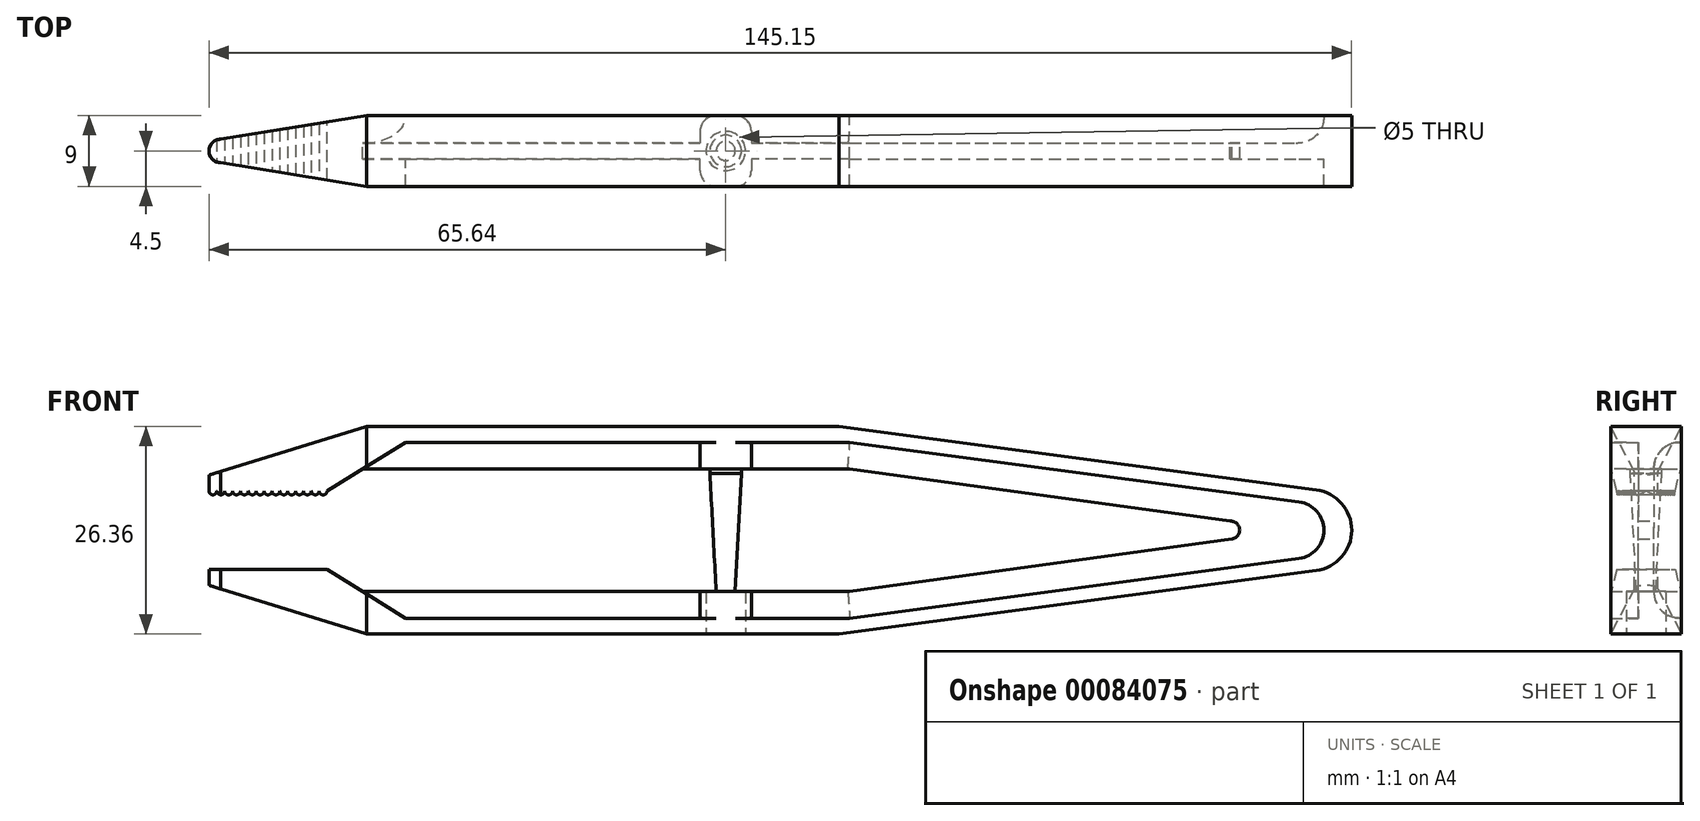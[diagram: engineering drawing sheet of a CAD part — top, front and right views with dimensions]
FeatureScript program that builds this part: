
annotation { "Feature Type Name" : "Feature", "Feature Type Description" : "" }
export const myFeature = defineFeature(function(context is Context, id is Id, definition is map)
    precondition{}
    {
        {
            var Q0;
            Q0=qCreatedBy(makeId("Front.planeOp"),FACE);
            var sketch = newSketch(context, id + "F0", { "sketchPlane" : qUnion([Q0])});
            skLineSegment(sketch, "E0", {"start": v(-60.1, 0) * mm, "end": v(64.63, 0) * mm});
            skLineSegment(sketch, "E1", {"start": v(-65.64, 7) * mm, "end": v(-45.64, 13.18) * mm});
            skLineSegment(sketch, "E2", {"start": v(-45.64, 13.18) * mm, "end": v(14.36, 13.18) * mm});
            skLineSegment(sketch, "E3", {"start": v(14.36, 13.18) * mm, "end": v(75.04, 5.1) * mm});
            skLineSegment(sketch, "E4", {"start": v(-65.64, 7) * mm, "end": v(-65.64, 5) * mm});
            skLineSegment(sketch, "E5", {"start": v(-65.64, 5) * mm, "end": v(-50.64, 5) * mm});
            skLineSegment(sketch, "E6", {"start": v(-50.64, 5) * mm, "end": v(-40.69, 11.18) * mm});
            skLineSegment(sketch, "E7", {"start": v(-40.69, 11.18) * mm, "end": v(15.75, 11.18) * mm});
            skLineSegment(sketch, "E8", {"start": v(15.75, 11.18) * mm, "end": v(72.84, 3.59) * mm});
            skLineSegment(sketch, "E9.MirrorCS", {"start": v(-65.64, -7) * mm, "end": v(-65.64, -5) * mm});
            skLineSegment(sketch, "E10.MirrorCS", {"start": v(-65.64, -5) * mm, "end": v(-50.64, -5) * mm});
            skLineSegment(sketch, "E11.MirrorCS", {"start": v(-45.64, -13.18) * mm, "end": v(14.36, -13.18) * mm});
            skLineSegment(sketch, "E12.MirrorCS", {"start": v(-40.69, -11.18) * mm, "end": v(15.75, -11.18) * mm});
            skLineSegment(sketch, "E13.MirrorCS", {"start": v(14.36, -13.18) * mm, "end": v(75.04, -5.1) * mm});
            skLineSegment(sketch, "E14.MirrorCS", {"start": v(-50.64, -5) * mm, "end": v(-40.69, -11.18) * mm});
            skLineSegment(sketch, "E15.MirrorCS", {"start": v(-65.64, -7) * mm, "end": v(-45.64, -13.18) * mm});
            skLineSegment(sketch, "E16.MirrorCS", {"start": v(15.75, -11.18) * mm, "end": v(72.84, -3.59) * mm});
            skArc(sketch, "E17", {"start": v(75.04, -5.1) * mm, "mid": v(79.51, 0) * mm, "end": v(75.04, 5.1) * mm});
            skArc(sketch, "E18", {"start": v(72.84, -3.59) * mm, "mid": v(75.98, 0) * mm, "end": v(72.84, 3.59) * mm});
            skLineSegment(sketch, "E19", {"start": v(15.75, 7.8) * mm, "end": v(-46.13, 7.8) * mm});
            skLineSegment(sketch, "E20", {"start": v(15.75, 7.8) * mm, "end": v(72.36, 0) * mm});
            skLineSegment(sketch, "E21.MirrorCS", {"start": v(15.75, -7.8) * mm, "end": v(-46.13, -7.8) * mm});
            skLineSegment(sketch, "E22.MirrorCS", {"start": v(15.75, -7.8) * mm, "end": v(72.36, 0) * mm});
            skArc(sketch, "E23", {"start": v(64.28, -1.11) * mm, "mid": v(65.28, 0.14) * mm, "end": v(64.03, 1.15) * mm});
            skSolve(sketch);
        }
        {
            var Q0;
            Q0=makeQuery(id+"F0.imprint","IMPRINT",FACE,{"disambiguationData":[TD([[makeQuery(id+"F0.imprint","IMPRINT",EDGE,{"derivedFrom":sQuery(id+"F0.wireOp",EDGE,"E1")}),-1.0]])]});
            extrude(context, id + "F1", {"entities" : qUnion([Q0]), "endBound" : BoundingType.SYMMETRIC, "depth" : 9 * mm});
        }
        {
            var Q0;
            {var subQ10=sQuery(id+"F0.wireOp",EDGE,"E7");Q0=makeQuery(id+"F0.imprint","IMPRINT",FACE,{"disambiguationData":[TD([[makeQuery(id+"F0.imprint","IMPRINT",EDGE,{"derivedFrom":subQ10}),-1.0]])]});}
            var Q1;
            {var subQ0=sQuery(id+"F0.wireOp",EDGE,"E22.MirrorCS");var subQ1=sQuery(id+"F0.wireOp",EDGE,"E20");var subQ2=makeQuery(id+"F0.imprint","INTERSECT",VERTEX,{"derivedFrom":[subQ1,subQ0]});Q1=makeQuery(id+"F0.imprint","IMPRINT",FACE,{"disambiguationData":[TD([[makeQuery(id+"F0.imprint","IMPRINT",EDGE,{"disambiguationData":[TD([[subQ2,1.0]])],"derivedFrom":subQ1}),-1.0]])]});}
            extrude(context, id + "F2", {"entities" : qUnion([Q0, Q1]), "operationType" : NewBodyOperationType.ADD, "endBound" : BoundingType.SYMMETRIC, "depth" : 2 * mm});
        }
        {
            var Q0;
            Q0=makeQuery(id+"F1.opExtrude","CAP_FACE",FACE,{"disambiguationData":[OSD([sQuery(id+"F0.wireOp",EDGE,"E1"),sQuery(id+"F0.wireOp",EDGE,"E2"),sQuery(id+"F0.wireOp",EDGE,"E3"),sQuery(id+"F0.wireOp",EDGE,"E4"),sQuery(id+"F0.wireOp",EDGE,"E5"),sQuery(id+"F0.wireOp",EDGE,"E6"),sQuery(id+"F0.wireOp",EDGE,"E7"),sQuery(id+"F0.wireOp",EDGE,"E8"),sQuery(id+"F0.wireOp",EDGE,"E9.MirrorCS"),sQuery(id+"F0.wireOp",EDGE,"E10.MirrorCS"),sQuery(id+"F0.wireOp",EDGE,"E11.MirrorCS"),sQuery(id+"F0.wireOp",EDGE,"E12.MirrorCS"),sQuery(id+"F0.wireOp",EDGE,"E13.MirrorCS"),sQuery(id+"F0.wireOp",EDGE,"E14.MirrorCS"),sQuery(id+"F0.wireOp",EDGE,"E15.MirrorCS"),sQuery(id+"F0.wireOp",EDGE,"E16.MirrorCS"),sQuery(id+"F0.wireOp",EDGE,"E17"),sQuery(id+"F0.wireOp",EDGE,"E18")])],"isStart":false});
            var sketch = newSketch(context, id + "F3", { "sketchPlane" : qUnion([Q0])});
            skLineSegment(sketch, "E24", {"start": v(-29.66, 0) * mm, "end": v(-67.82, 0) * mm});
            skArc(sketch, "E25", {"start": v(-65.64, 5) * mm, "mid": v(-65.14, 4.5) * mm, "end": v(-64.64, 5) * mm});
            skArc(sketch, "E26.1.0.0", {"start": v(-64.64, 5) * mm, "mid": v(-64.14, 4.5) * mm, "end": v(-63.64, 5) * mm});
            skArc(sketch, "E26.2.0.0", {"start": v(-63.64, 5) * mm, "mid": v(-63.14, 4.5) * mm, "end": v(-62.64, 5) * mm});
            skArc(sketch, "E26.3.0.0", {"start": v(-62.64, 5) * mm, "mid": v(-62.14, 4.5) * mm, "end": v(-61.64, 5) * mm});
            skArc(sketch, "E26.4.0.0", {"start": v(-61.64, 5) * mm, "mid": v(-61.14, 4.5) * mm, "end": v(-60.64, 5) * mm});
            skArc(sketch, "E26.5.0.0", {"start": v(-60.64, 5) * mm, "mid": v(-60.14, 4.5) * mm, "end": v(-59.64, 5) * mm});
            skArc(sketch, "E26.6.0.0", {"start": v(-59.64, 5) * mm, "mid": v(-59.14, 4.5) * mm, "end": v(-58.64, 5) * mm});
            skArc(sketch, "E26.7.0.0", {"start": v(-58.64, 5) * mm, "mid": v(-58.14, 4.5) * mm, "end": v(-57.64, 5) * mm});
            skArc(sketch, "E26.8.0.0", {"start": v(-57.64, 5) * mm, "mid": v(-57.14, 4.5) * mm, "end": v(-56.64, 5) * mm});
            skArc(sketch, "E26.9.0.0", {"start": v(-56.64, 5) * mm, "mid": v(-56.14, 4.5) * mm, "end": v(-55.64, 5) * mm});
            skArc(sketch, "E26.10.0.0", {"start": v(-55.64, 5) * mm, "mid": v(-55.14, 4.5) * mm, "end": v(-54.64, 5) * mm});
            skArc(sketch, "E26.11.0.0", {"start": v(-54.64, 5) * mm, "mid": v(-54.14, 4.5) * mm, "end": v(-53.64, 5) * mm});
            skArc(sketch, "E26.12.0.0", {"start": v(-53.64, 5) * mm, "mid": v(-53.14, 4.5) * mm, "end": v(-52.64, 5) * mm});
            skArc(sketch, "E26.13.0.0", {"start": v(-52.64, 5) * mm, "mid": v(-52.14, 4.5) * mm, "end": v(-51.64, 5) * mm});
            skArc(sketch, "E26.14.0.0", {"start": v(-51.64, 5) * mm, "mid": v(-51.14, 4.5) * mm, "end": v(-50.64, 5) * mm});
            skLineSegment(sketch, "E26.direction1", {"start": v(-65.64, 5) * mm, "end": v(-64.64, 5) * mm, "construction": true});
            skLineSegment(sketch, "E27.MirrorCS", {"start": v(-65.64, -5) * mm, "end": v(-64.64, -5) * mm, "construction": true});
            skArc(sketch, "E28.MirrorCS", {"start": v(-53.64, -5) * mm, "mid": v(-53.14, -4.5) * mm, "end": v(-52.64, -5) * mm});
            skArc(sketch, "E29.MirrorCS", {"start": v(-52.64, -5) * mm, "mid": v(-52.14, -4.5) * mm, "end": v(-51.64, -5) * mm});
            skArc(sketch, "E30.MirrorCS", {"start": v(-51.64, -5) * mm, "mid": v(-51.14, -4.5) * mm, "end": v(-50.64, -5) * mm});
            skArc(sketch, "E31.MirrorCS", {"start": v(-65.64, -5) * mm, "mid": v(-65.14, -4.5) * mm, "end": v(-64.64, -5) * mm});
            skArc(sketch, "E32.MirrorCS", {"start": v(-64.64, -5) * mm, "mid": v(-64.14, -4.5) * mm, "end": v(-63.64, -5) * mm});
            skArc(sketch, "E33.MirrorCS", {"start": v(-63.64, -5) * mm, "mid": v(-63.14, -4.5) * mm, "end": v(-62.64, -5) * mm});
            skArc(sketch, "E34.MirrorCS", {"start": v(-62.64, -5) * mm, "mid": v(-62.14, -4.5) * mm, "end": v(-61.64, -5) * mm});
            skArc(sketch, "E35.MirrorCS", {"start": v(-61.64, -5) * mm, "mid": v(-61.14, -4.5) * mm, "end": v(-60.64, -5) * mm});
            skArc(sketch, "E36.MirrorCS", {"start": v(-60.64, -5) * mm, "mid": v(-60.14, -4.5) * mm, "end": v(-59.64, -5) * mm});
            skArc(sketch, "E37.MirrorCS", {"start": v(-59.64, -5) * mm, "mid": v(-59.14, -4.5) * mm, "end": v(-58.64, -5) * mm});
            skArc(sketch, "E38.MirrorCS", {"start": v(-58.64, -5) * mm, "mid": v(-58.14, -4.5) * mm, "end": v(-57.64, -5) * mm});
            skArc(sketch, "E39.MirrorCS", {"start": v(-57.64, -5) * mm, "mid": v(-57.14, -4.5) * mm, "end": v(-56.64, -5) * mm});
            skArc(sketch, "E40.MirrorCS", {"start": v(-56.64, -5) * mm, "mid": v(-56.14, -4.5) * mm, "end": v(-55.64, -5) * mm});
            skArc(sketch, "E41.MirrorCS", {"start": v(-55.64, -5) * mm, "mid": v(-55.14, -4.5) * mm, "end": v(-54.64, -5) * mm});
            skArc(sketch, "E42.MirrorCS", {"start": v(-54.64, -5) * mm, "mid": v(-54.14, -4.5) * mm, "end": v(-53.64, -5) * mm});
            skSolve(sketch);
        }
        {
            var Q0;
            {var subQ0=sQuery(id+"F3.wireOp",EDGE,"E25");Q0=makeQuery(id+"F3.imprint","IMPRINT",FACE,{"disambiguationData":[TD([[makeQuery(id+"F3.imprint","IMPRINT",EDGE,{"derivedFrom":subQ0}),1.0]])]});}
            var Q1;
            {var subQ0=sQuery(id+"F3.wireOp",EDGE,"E26.1.0.0");Q1=makeQuery(id+"F3.imprint","IMPRINT",FACE,{"disambiguationData":[TD([[makeQuery(id+"F3.imprint","IMPRINT",EDGE,{"derivedFrom":subQ0}),1.0]])]});}
            var Q2;
            {var subQ0=sQuery(id+"F3.wireOp",EDGE,"E26.2.0.0");Q2=makeQuery(id+"F3.imprint","IMPRINT",FACE,{"disambiguationData":[TD([[makeQuery(id+"F3.imprint","IMPRINT",EDGE,{"derivedFrom":subQ0}),1.0]])]});}
            var Q3;
            {var subQ0=sQuery(id+"F3.wireOp",EDGE,"E26.3.0.0");Q3=makeQuery(id+"F3.imprint","IMPRINT",FACE,{"disambiguationData":[TD([[makeQuery(id+"F3.imprint","IMPRINT",EDGE,{"derivedFrom":subQ0}),1.0]])]});}
            var Q4;
            {var subQ0=sQuery(id+"F3.wireOp",EDGE,"E26.4.0.0");Q4=makeQuery(id+"F3.imprint","IMPRINT",FACE,{"disambiguationData":[TD([[makeQuery(id+"F3.imprint","IMPRINT",EDGE,{"derivedFrom":subQ0}),1.0]])]});}
            var Q5;
            {var subQ0=sQuery(id+"F3.wireOp",EDGE,"E26.5.0.0");Q5=makeQuery(id+"F3.imprint","IMPRINT",FACE,{"disambiguationData":[TD([[makeQuery(id+"F3.imprint","IMPRINT",EDGE,{"derivedFrom":subQ0}),1.0]])]});}
            var Q6;
            {var subQ0=sQuery(id+"F3.wireOp",EDGE,"E26.6.0.0");Q6=makeQuery(id+"F3.imprint","IMPRINT",FACE,{"disambiguationData":[TD([[makeQuery(id+"F3.imprint","IMPRINT",EDGE,{"derivedFrom":subQ0}),1.0]])]});}
            var Q7;
            {var subQ0=sQuery(id+"F3.wireOp",EDGE,"E26.7.0.0");Q7=makeQuery(id+"F3.imprint","IMPRINT",FACE,{"disambiguationData":[TD([[makeQuery(id+"F3.imprint","IMPRINT",EDGE,{"derivedFrom":subQ0}),1.0]])]});}
            var Q8;
            {var subQ0=sQuery(id+"F3.wireOp",EDGE,"E26.8.0.0");Q8=makeQuery(id+"F3.imprint","IMPRINT",FACE,{"disambiguationData":[TD([[makeQuery(id+"F3.imprint","IMPRINT",EDGE,{"derivedFrom":subQ0}),1.0]])]});}
            var Q9;
            {var subQ0=sQuery(id+"F3.wireOp",EDGE,"E26.9.0.0");Q9=makeQuery(id+"F3.imprint","IMPRINT",FACE,{"disambiguationData":[TD([[makeQuery(id+"F3.imprint","IMPRINT",EDGE,{"derivedFrom":subQ0}),1.0]])]});}
            var Q10;
            {var subQ0=sQuery(id+"F3.wireOp",EDGE,"E26.10.0.0");Q10=makeQuery(id+"F3.imprint","IMPRINT",FACE,{"disambiguationData":[TD([[makeQuery(id+"F3.imprint","IMPRINT",EDGE,{"derivedFrom":subQ0}),1.0]])]});}
            var Q11;
            {var subQ0=sQuery(id+"F3.wireOp",EDGE,"E26.11.0.0");Q11=makeQuery(id+"F3.imprint","IMPRINT",FACE,{"disambiguationData":[TD([[makeQuery(id+"F3.imprint","IMPRINT",EDGE,{"derivedFrom":subQ0}),1.0]])]});}
            var Q12;
            {var subQ0=sQuery(id+"F3.wireOp",EDGE,"E26.12.0.0");Q12=makeQuery(id+"F3.imprint","IMPRINT",FACE,{"disambiguationData":[TD([[makeQuery(id+"F3.imprint","IMPRINT",EDGE,{"derivedFrom":subQ0}),1.0]])]});}
            var Q13;
            {var subQ0=sQuery(id+"F3.wireOp",EDGE,"E26.13.0.0");Q13=makeQuery(id+"F3.imprint","IMPRINT",FACE,{"disambiguationData":[TD([[makeQuery(id+"F3.imprint","IMPRINT",EDGE,{"derivedFrom":subQ0}),1.0]])]});}
            var Q14;
            {var subQ0=sQuery(id+"F3.wireOp",EDGE,"E26.14.0.0");Q14=makeQuery(id+"F3.imprint","IMPRINT",FACE,{"disambiguationData":[TD([[makeQuery(id+"F3.imprint","IMPRINT",EDGE,{"derivedFrom":subQ0}),1.0]])]});}
            var Q15;
            {var subQ0=sQuery(id+"F3.wireOp",EDGE,"E31.MirrorCS");Q15=makeQuery(id+"F3.imprint","IMPRINT",FACE,{"disambiguationData":[TD([[makeQuery(id+"F3.imprint","IMPRINT",EDGE,{"derivedFrom":subQ0}),-1.0]])]});}
            var Q16;
            {var subQ0=sQuery(id+"F3.wireOp",EDGE,"E32.MirrorCS");Q16=makeQuery(id+"F3.imprint","IMPRINT",FACE,{"disambiguationData":[TD([[makeQuery(id+"F3.imprint","IMPRINT",EDGE,{"derivedFrom":subQ0}),-1.0]])]});}
            var Q17;
            {var subQ0=sQuery(id+"F3.wireOp",EDGE,"E33.MirrorCS");Q17=makeQuery(id+"F3.imprint","IMPRINT",FACE,{"disambiguationData":[TD([[makeQuery(id+"F3.imprint","IMPRINT",EDGE,{"derivedFrom":subQ0}),-1.0]])]});}
            var Q18;
            {var subQ0=sQuery(id+"F3.wireOp",EDGE,"E34.MirrorCS");Q18=makeQuery(id+"F3.imprint","IMPRINT",FACE,{"disambiguationData":[TD([[makeQuery(id+"F3.imprint","IMPRINT",EDGE,{"derivedFrom":subQ0}),-1.0]])]});}
            var Q19;
            {var subQ0=sQuery(id+"F3.wireOp",EDGE,"E35.MirrorCS");Q19=makeQuery(id+"F3.imprint","IMPRINT",FACE,{"disambiguationData":[TD([[makeQuery(id+"F3.imprint","IMPRINT",EDGE,{"derivedFrom":subQ0}),-1.0]])]});}
            var Q20;
            {var subQ0=sQuery(id+"F3.wireOp",EDGE,"E36.MirrorCS");Q20=makeQuery(id+"F3.imprint","IMPRINT",FACE,{"disambiguationData":[TD([[makeQuery(id+"F3.imprint","IMPRINT",EDGE,{"derivedFrom":subQ0}),-1.0]])]});}
            var Q21;
            {var subQ0=sQuery(id+"F3.wireOp",EDGE,"E37.MirrorCS");Q21=makeQuery(id+"F3.imprint","IMPRINT",FACE,{"disambiguationData":[TD([[makeQuery(id+"F3.imprint","IMPRINT",EDGE,{"derivedFrom":subQ0}),-1.0]])]});}
            var Q22;
            {var subQ0=sQuery(id+"F3.wireOp",EDGE,"E38.MirrorCS");Q22=makeQuery(id+"F3.imprint","IMPRINT",FACE,{"disambiguationData":[TD([[makeQuery(id+"F3.imprint","IMPRINT",EDGE,{"derivedFrom":subQ0}),-1.0]])]});}
            var Q23;
            {var subQ0=sQuery(id+"F3.wireOp",EDGE,"E39.MirrorCS");Q23=makeQuery(id+"F3.imprint","IMPRINT",FACE,{"disambiguationData":[TD([[makeQuery(id+"F3.imprint","IMPRINT",EDGE,{"derivedFrom":subQ0}),-1.0]])]});}
            var Q24;
            {var subQ0=sQuery(id+"F3.wireOp",EDGE,"E40.MirrorCS");Q24=makeQuery(id+"F3.imprint","IMPRINT",FACE,{"disambiguationData":[TD([[makeQuery(id+"F3.imprint","IMPRINT",EDGE,{"derivedFrom":subQ0}),-1.0]])]});}
            var Q25;
            {var subQ0=sQuery(id+"F3.wireOp",EDGE,"E41.MirrorCS");Q25=makeQuery(id+"F3.imprint","IMPRINT",FACE,{"disambiguationData":[TD([[makeQuery(id+"F3.imprint","IMPRINT",EDGE,{"derivedFrom":subQ0}),-1.0]])]});}
            var Q26;
            {var subQ0=sQuery(id+"F3.wireOp",EDGE,"E42.MirrorCS");Q26=makeQuery(id+"F3.imprint","IMPRINT",FACE,{"disambiguationData":[TD([[makeQuery(id+"F3.imprint","IMPRINT",EDGE,{"derivedFrom":subQ0}),-1.0]])]});}
            var Q27;
            {var subQ0=sQuery(id+"F3.wireOp",EDGE,"E28.MirrorCS");Q27=makeQuery(id+"F3.imprint","IMPRINT",FACE,{"disambiguationData":[TD([[makeQuery(id+"F3.imprint","IMPRINT",EDGE,{"derivedFrom":subQ0}),-1.0]])]});}
            var Q28;
            {var subQ0=sQuery(id+"F3.wireOp",EDGE,"E29.MirrorCS");Q28=makeQuery(id+"F3.imprint","IMPRINT",FACE,{"disambiguationData":[TD([[makeQuery(id+"F3.imprint","IMPRINT",EDGE,{"derivedFrom":subQ0}),-1.0]])]});}
            var Q29;
            {var subQ0=sQuery(id+"F3.wireOp",EDGE,"E30.MirrorCS");Q29=makeQuery(id+"F3.imprint","IMPRINT",FACE,{"disambiguationData":[TD([[makeQuery(id+"F3.imprint","IMPRINT",EDGE,{"derivedFrom":subQ0}),-1.0]])]});}
            var Q30;
            Q30=makeQuery(id+"F1.opExtrude","CAP_FACE",FACE,{"disambiguationData":[OSD([sQuery(id+"F0.wireOp",EDGE,"E1"),sQuery(id+"F0.wireOp",EDGE,"E2"),sQuery(id+"F0.wireOp",EDGE,"E3"),sQuery(id+"F0.wireOp",EDGE,"E4"),sQuery(id+"F0.wireOp",EDGE,"E5"),sQuery(id+"F0.wireOp",EDGE,"E6"),sQuery(id+"F0.wireOp",EDGE,"E7"),sQuery(id+"F0.wireOp",EDGE,"E8"),sQuery(id+"F0.wireOp",EDGE,"E9.MirrorCS"),sQuery(id+"F0.wireOp",EDGE,"E10.MirrorCS"),sQuery(id+"F0.wireOp",EDGE,"E11.MirrorCS"),sQuery(id+"F0.wireOp",EDGE,"E12.MirrorCS"),sQuery(id+"F0.wireOp",EDGE,"E13.MirrorCS"),sQuery(id+"F0.wireOp",EDGE,"E14.MirrorCS"),sQuery(id+"F0.wireOp",EDGE,"E15.MirrorCS"),sQuery(id+"F0.wireOp",EDGE,"E16.MirrorCS"),sQuery(id+"F0.wireOp",EDGE,"E17"),sQuery(id+"F0.wireOp",EDGE,"E18")])],"isStart":true});
            extrude(context, id + "F4", {"entities" : qUnion([Q0, Q1, Q2, Q3, Q4, Q5, Q6, Q7, Q8, Q9, Q10, Q11, Q12, Q13, Q14, Q15, Q16, Q17, Q18, Q19, Q20, Q21, Q22, Q23, Q24, Q25, Q26, Q27, Q28, Q29]), "operationType" : NewBodyOperationType.ADD, "endBound" : BoundingType.UP_TO_SURFACE, "oppositeDirection" : true, "endBoundEntityFace" : qUnion([Q30]), "depth" : 9 * mm});
        }
        {
            var Q0;
            Q0=makeQuery(id+"F2.opExtrude","CAP_EDGE",EDGE,{"disambiguationData":[OSD([sQuery(id+"F0.wireOp",EDGE,"E6")])],"isStart":false});
            var Q1;
            Q1=makeQuery(id+"F2.opExtrude","CAP_EDGE",EDGE,{"disambiguationData":[OSD([sQuery(id+"F0.wireOp",EDGE,"E7")])],"isStart":false});
            var Q2;
            Q2=makeQuery(id+"F2.opExtrude","CAP_EDGE",EDGE,{"disambiguationData":[OSD([sQuery(id+"F0.wireOp",EDGE,"E8")])],"isStart":false});
            var Q3;
            Q3=makeQuery(id+"F2.opExtrude","CAP_EDGE",EDGE,{"disambiguationData":[OSD([sQuery(id+"F0.wireOp",EDGE,"E18")])],"isStart":false});
            var Q4;
            Q4=makeQuery(id+"F2.opExtrude","CAP_EDGE",EDGE,{"disambiguationData":[OSD([sQuery(id+"F0.wireOp",EDGE,"E16.MirrorCS")])],"isStart":false});
            var Q5;
            Q5=makeQuery(id+"F2.opExtrude","CAP_EDGE",EDGE,{"disambiguationData":[OSD([sQuery(id+"F0.wireOp",EDGE,"E12.MirrorCS")])],"isStart":false});
            var Q6;
            Q6=makeQuery(id+"F2.opExtrude","CAP_EDGE",EDGE,{"disambiguationData":[OSD([sQuery(id+"F0.wireOp",EDGE,"E14.MirrorCS")])],"isStart":false});
            var Q7;
            Q7=makeQuery(id+"F2.opExtrude","CAP_EDGE",EDGE,{"disambiguationData":[OSD([sQuery(id+"F0.wireOp",EDGE,"E8")])],"isStart":true});
            var Q8;
            Q8=makeQuery(id+"F2.opExtrude","CAP_EDGE",EDGE,{"disambiguationData":[OSD([sQuery(id+"F0.wireOp",EDGE,"E7")])],"isStart":true});
            var Q9;
            Q9=makeQuery(id+"F2.opExtrude","CAP_EDGE",EDGE,{"disambiguationData":[OSD([sQuery(id+"F0.wireOp",EDGE,"E6")])],"isStart":true});
            var Q10;
            Q10=makeQuery(id+"F2.opExtrude","CAP_EDGE",EDGE,{"disambiguationData":[OSD([sQuery(id+"F0.wireOp",EDGE,"E14.MirrorCS")])],"isStart":true});
            var Q11;
            Q11=makeQuery(id+"F2.opExtrude","CAP_EDGE",EDGE,{"disambiguationData":[OSD([sQuery(id+"F0.wireOp",EDGE,"E12.MirrorCS")])],"isStart":true});
            var Q12;
            Q12=makeQuery(id+"F2.opExtrude","CAP_EDGE",EDGE,{"disambiguationData":[OSD([sQuery(id+"F0.wireOp",EDGE,"E16.MirrorCS")])],"isStart":true});
            var Q13;
            Q13=makeQuery(id+"F2.opExtrude","CAP_EDGE",EDGE,{"disambiguationData":[OSD([sQuery(id+"F0.wireOp",EDGE,"E18")])],"isStart":true});
            fillet(context, id + "F5", {"entities" : qUnion([Q0, Q1, Q2, Q3, Q4, Q5, Q6, Q7, Q8, Q9, Q10, Q11, Q12, Q13]), "radius" : 3.3 * mm, "tangentPropagation" : true, "allowEdgeOverflow" : false});
        }
        {
            var Q0;
            Q0=qCreatedBy(makeId("Top.planeOp"),FACE);
            var sketch = newSketch(context, id + "F6", { "sketchPlane" : qUnion([Q0])});
            skLineSegment(sketch, "E43", {"start": v(0, 0) * mm, "end": v(-65.64, 0) * mm});
            skCircle(sketch, "E44", {"center": v(-64.14, 0) * mm, "radius": 1.5 * mm});
            skLineSegment(sketch, "E45", {"start": v(-25.64, 0) * mm, "end": v(-25.64, -4.5) * mm});
            skLineSegment(sketch, "E46", {"start": v(-64.14, 0) * mm, "end": v(-64.14, -1.5) * mm});
            skLineSegment(sketch, "E47.MirrorCS", {"start": v(-25.64, 0) * mm, "end": v(-25.64, 4.5) * mm});
            skLineSegment(sketch, "E48", {"start": v(-25.64, -4.5) * mm, "end": v(-65.64, -4.5) * mm});
            skLineSegment(sketch, "E49", {"start": v(-65.64, 0) * mm, "end": v(-65.64, -4.5) * mm});
            skLineSegment(sketch, "E50.MirrorCS", {"start": v(-25.64, 4.5) * mm, "end": v(-65.64, 4.5) * mm});
            skLineSegment(sketch, "E51.MirrorCS", {"start": v(-65.64, 0) * mm, "end": v(-65.64, 4.5) * mm});
            skLineSegment(sketch, "E52.0", {"start": v(-45.64, -4.5) * mm, "end": v(-45.64, 4.5) * mm});
            skLineSegment(sketch, "E53", {"start": v(-64.14, 1.5) * mm, "end": v(-45.64, 4.5) * mm});
            skLineSegment(sketch, "E54", {"start": v(-64.14, -1.5) * mm, "end": v(-45.64, -4.5) * mm});
            skSolve(sketch);
        }
        {
            var Q0;
            {var subQ0=sQuery(id+"F6.wireOp",EDGE,"E51.MirrorCS");Q0=makeQuery(id+"F6.imprint","IMPRINT",FACE,{"disambiguationData":[TD([[makeQuery(id+"F6.imprint","IMPRINT",EDGE,{"derivedFrom":subQ0}),-1.0]])]});}
            var Q1;
            {var subQ0=sQuery(id+"F6.wireOp",EDGE,"E49");Q1=makeQuery(id+"F6.imprint","IMPRINT",FACE,{"disambiguationData":[TD([[makeQuery(id+"F6.imprint","IMPRINT",EDGE,{"derivedFrom":subQ0}),1.0]])]});}
            extrude(context, id + "F7", {"entities" : qUnion([Q0, Q1]), "operationType" : NewBodyOperationType.REMOVE, "endBound" : BoundingType.SYMMETRIC, "oppositeDirection" : true, "depth" : 46.93 * mm});
        }
        {
            var Q0;
            Q0=makeQuery(id+"F1.opExtrude","SWEPT_FACE",FACE,{"disambiguationData":[OSD([sQuery(id+"F0.wireOp",EDGE,"E11.MirrorCS")])]});
            var sketch = newSketch(context, id + "F8", { "sketchPlane" : qUnion([Q0])});
            skCircle(sketch, "E55", {"center": v(0, 0) * mm, "radius": 2.5 * mm});
            skCircle(sketch, "E56", {"center": v(0, 0) * mm, "radius": 3.25 * mm});
            skLineSegment(sketch, "E57", {"start": v(0, 4.5) * mm, "end": v(0, -4.5) * mm, "construction": true});
            skLineSegment(sketch, "E58", {"start": v(-3.25, 4.5) * mm, "end": v(-3.25, -4.5) * mm});
            skLineSegment(sketch, "E59.MirrorCS", {"start": v(3.25, 4.5) * mm, "end": v(3.25, -4.5) * mm});
            skSolve(sketch);
        }
        {
            var Q0;
            Q0=makeQuery(id+"F8.imprint","IMPRINT",FACE,{"disambiguationData":[TD([[makeQuery(id+"F8.imprint","IMPRINT",EDGE,{"derivedFrom":sQuery(id+"F8.wireOp",EDGE,"E55")}),1.0]])]});
            extrude(context, id + "F9", {"entities" : qUnion([Q0]), "operationType" : NewBodyOperationType.REMOVE, "endBound" : BoundingType.UP_TO_NEXT, "oppositeDirection" : true, "depth" : 25 * mm});
        }
        {
            var Q0;
            Q0=makeQuery(id+"F8.imprint","IMPRINT",FACE,{"disambiguationData":[TD([[makeQuery(id+"F8.imprint","IMPRINT",EDGE,{"derivedFrom":sQuery(id+"F8.wireOp",EDGE,"E55")}),-1.0]])]});
            var Q1;
            {var subQ0=sQuery(id+"F8.wireOp",EDGE,"E58");var subQ1=sQuery(id+"F8.wireOp",EDGE,"E56");var subQ2=makeQuery(id+"F8.imprint","INTERSECT",VERTEX,{"derivedFrom":[subQ1,subQ0]});Q1=makeQuery(id+"F8.imprint","IMPRINT",FACE,{"disambiguationData":[TD([[makeQuery(id+"F8.imprint","IMPRINT",EDGE,{"disambiguationData":[TD([[subQ2,1.0]])],"derivedFrom":subQ1}),-1.0]])]});}
            var Q2;
            {var subQ0=sQuery(id+"F8.wireOp",EDGE,"E58");var subQ1=sQuery(id+"F8.wireOp",EDGE,"E56");var subQ2=makeQuery(id+"F8.imprint","INTERSECT",VERTEX,{"derivedFrom":[subQ1,subQ0]});Q2=makeQuery(id+"F8.imprint","IMPRINT",FACE,{"disambiguationData":[TD([[makeQuery(id+"F8.imprint","IMPRINT",EDGE,{"disambiguationData":[TD([[subQ2,-1.0]])],"derivedFrom":subQ1}),-1.0]])]});}
            var Q3;
            {var subQ2=sQuery(id+"F0.wireOp",EDGE,"E21.MirrorCS");var subQ7=sQuery(id+"F0.wireOp",EDGE,"E14.MirrorCS");Q3=makeQuery(id+"F9.boolean.opBoolean","SPLIT",FACE,{"disambiguationData":[TD([makeQuery(id+"F1.opExtrude","SWEPT_FACE",FACE,{"disambiguationData":[OSD([subQ7])]})])],"derivedFrom":makeQuery(id+"F2.opExtrude","SWEPT_FACE",FACE,{"disambiguationData":[OSD([subQ2])]})});}
            extrude(context, id + "F10", {"entities" : qUnion([Q0, Q1, Q2]), "operationType" : NewBodyOperationType.ADD, "endBound" : BoundingType.UP_TO_SURFACE, "oppositeDirection" : true, "endBoundEntityFace" : qUnion([Q3]), "depth" : 25 * mm});
        }
        {
            var Q0;
            Q0=makeQuery(id+"F1.opExtrude","SWEPT_FACE",FACE,{"disambiguationData":[OSD([sQuery(id+"F0.wireOp",EDGE,"E2")])]});
            var sketch = newSketch(context, id + "F11", { "sketchPlane" : qUnion([Q0])});
            skCircle(sketch, "E60", {"center": v(0, 0) * mm, "radius": 2 * mm});
            skLineSegment(sketch, "E61.0", {"start": v(-3.25, -4.5) * mm, "end": v(-3.25, 4.5) * mm});
            skLineSegment(sketch, "E62.0", {"start": v(3.25, -4.5) * mm, "end": v(3.25, 4.5) * mm});
            skSolve(sketch);
        }
        {
            var Q0;
            Q0 = qSketchRegion(id + "F11", true);
            var Q1;
            {var subQ0=sQuery(id+"F8.wireOp",EDGE,"E55");var subQ2=sQuery(id+"F0.wireOp",EDGE,"E22.MirrorCS");var subQ3=sQuery(id+"F0.wireOp",EDGE,"E21.MirrorCS");var subQ8=sQuery(id+"F0.wireOp",EDGE,"E14.MirrorCS");var subQ16=makeQuery(id+"F2.opExtrude","SWEPT_FACE",FACE,{"disambiguationData":[OSD([subQ3])]});Q1=makeQuery(id+"F10.boolean.opBoolean","MERGE",FACE,{"derivedFrom":[makeQuery(id+"F9.boolean.opBoolean","SPLIT",FACE,{"disambiguationData":[TD([makeQuery(id+"F2.opExtrude","SWEPT_FACE",FACE,{"disambiguationData":[OSD([subQ2])]})])],"derivedFrom":subQ16}),makeQuery(id+"F9.boolean.opBoolean","SPLIT",FACE,{"disambiguationData":[TD([makeQuery(id+"F1.opExtrude","SWEPT_FACE",FACE,{"disambiguationData":[OSD([subQ8])]})])],"derivedFrom":subQ16}),makeQuery(id+"F10.opExtrude","CAP_FACE",FACE,{"disambiguationData":[OSD([sQuery(id+"F0.wireOp",EDGE,"E11.MirrorCS"),subQ0,sQuery(id+"F8.wireOp",EDGE,"E58"),sQuery(id+"F8.wireOp",EDGE,"E59.MirrorCS")])],"isStart":false})]});}
            extrude(context, id + "F12", {"entities" : qUnion([Q0]), "operationType" : NewBodyOperationType.ADD, "endBound" : BoundingType.UP_TO_SURFACE, "oppositeDirection" : true, "endBoundEntityFace" : qUnion([Q1]), "depth" : 25 * mm});
        }
        {
            var Q0;
            Q0=makeQuery(id+"F12.opExtrude","CAP_EDGE",EDGE,{"disambiguationData":[OSD([sQuery(id+"F11.wireOp",EDGE,"E60")])],"isStart":false});
            chamfer(context, id + "F13", {"entities" : qUnion([Q0]), "chamferType" : ChamferType.OFFSET_ANGLE, "width" : 15 * mm, "oppositeDirection" : false, "angle" : 3 * degree, "tangentPropagation" : true});
        }
        {
            var Q0;
            Q0 = qSketchRegion(id + "F11", true);
            var Q1;
            Q1=makeQuery(id+"F11.imprint","IMPRINT",FACE,{"disambiguationData":[TD([[makeQuery(id+"F11.imprint","IMPRINT",EDGE,{"derivedFrom":sQuery(id+"F11.wireOp",EDGE,"E60")}),-1.0]])]});
            var Q2;
            {var subQ3=sQuery(id+"F0.wireOp",EDGE,"E20");var subQ4=sQuery(id+"F0.wireOp",EDGE,"E19");Q2=makeQuery(id+"F12.boolean.opBoolean","SPLIT",FACE,{"disambiguationData":[TD([makeQuery(id+"F2.opExtrude","SWEPT_FACE",FACE,{"disambiguationData":[OSD([subQ3])]})])],"derivedFrom":makeQuery(id+"F2.opExtrude","SWEPT_FACE",FACE,{"disambiguationData":[OSD([subQ4])]})});}
            extrude(context, id + "F14", {"entities" : qUnion([Q0, Q1]), "operationType" : NewBodyOperationType.ADD, "endBound" : BoundingType.UP_TO_SURFACE, "oppositeDirection" : true, "endBoundEntityFace" : qUnion([Q2]), "depth" : 25 * mm});
        }
        {
            var Q0;
            {var subQ0=sQuery(id+"F8.wireOp",EDGE,"E59.MirrorCS");var subQ1=sQuery(id+"F0.wireOp",EDGE,"E11.MirrorCS");Q0=makeQuery(id+"F10.opExtrude","SWEPT_EDGE",EDGE,{"disambiguationData":[OSD([subQ1,subQ0]),TDD([makeQuery(id+"F8.imprint","INTERSECT",VERTEX,{"derivedFrom":[makeQuery(id+"F1.opExtrude","CAP_EDGE",EDGE,{"disambiguationData":[OSD([subQ1])],"isStart":false}),subQ0]})])]});}
            var Q1;
            {var subQ0=sQuery(id+"F8.wireOp",EDGE,"E58");var subQ1=sQuery(id+"F0.wireOp",EDGE,"E11.MirrorCS");Q1=makeQuery(id+"F10.opExtrude","SWEPT_EDGE",EDGE,{"disambiguationData":[OSD([subQ1,subQ0]),TDD([makeQuery(id+"F8.imprint","INTERSECT",VERTEX,{"derivedFrom":[makeQuery(id+"F1.opExtrude","CAP_EDGE",EDGE,{"disambiguationData":[OSD([subQ1])],"isStart":false}),subQ0]})])]});}
            var Q2;
            {var subQ0=sQuery(id+"F8.wireOp",EDGE,"E59.MirrorCS");var subQ1=sQuery(id+"F0.wireOp",EDGE,"E11.MirrorCS");Q2=makeQuery(id+"F10.opExtrude","SWEPT_EDGE",EDGE,{"disambiguationData":[OSD([subQ1,subQ0]),TDD([makeQuery(id+"F8.imprint","INTERSECT",VERTEX,{"derivedFrom":[makeQuery(id+"F1.opExtrude","CAP_EDGE",EDGE,{"disambiguationData":[OSD([subQ1])],"isStart":true}),subQ0]})])]});}
            var Q3;
            {var subQ0=sQuery(id+"F8.wireOp",EDGE,"E58");var subQ1=sQuery(id+"F0.wireOp",EDGE,"E11.MirrorCS");Q3=makeQuery(id+"F10.opExtrude","SWEPT_EDGE",EDGE,{"disambiguationData":[OSD([subQ1,subQ0]),TDD([makeQuery(id+"F8.imprint","INTERSECT",VERTEX,{"derivedFrom":[makeQuery(id+"F1.opExtrude","CAP_EDGE",EDGE,{"disambiguationData":[OSD([subQ1])],"isStart":true}),subQ0]})])]});}
            var Q4;
            {var subQ0=sQuery(id+"F11.wireOp",EDGE,"E61.0");var subQ1=sQuery(id+"F0.wireOp",EDGE,"E2");Q4=makeQuery(id+"F14.opExtrude","SWEPT_EDGE",EDGE,{"disambiguationData":[OSD([subQ1,subQ0]),TDD([makeQuery(id+"F11.imprint","INTERSECT",VERTEX,{"derivedFrom":[makeQuery(id+"F1.opExtrude","CAP_EDGE",EDGE,{"disambiguationData":[OSD([subQ1])],"isStart":true}),subQ0]})])]});}
            var Q5;
            {var subQ0=sQuery(id+"F11.wireOp",EDGE,"E62.0");var subQ1=sQuery(id+"F0.wireOp",EDGE,"E2");Q5=makeQuery(id+"F14.opExtrude","SWEPT_EDGE",EDGE,{"disambiguationData":[OSD([subQ1,subQ0]),TDD([makeQuery(id+"F11.imprint","INTERSECT",VERTEX,{"derivedFrom":[makeQuery(id+"F1.opExtrude","CAP_EDGE",EDGE,{"disambiguationData":[OSD([subQ1])],"isStart":true}),subQ0]})])]});}
            var Q6;
            {var subQ0=sQuery(id+"F11.wireOp",EDGE,"E61.0");var subQ1=sQuery(id+"F0.wireOp",EDGE,"E2");Q6=makeQuery(id+"F14.opExtrude","SWEPT_EDGE",EDGE,{"disambiguationData":[OSD([subQ1,subQ0]),TDD([makeQuery(id+"F11.imprint","INTERSECT",VERTEX,{"derivedFrom":[makeQuery(id+"F1.opExtrude","CAP_EDGE",EDGE,{"disambiguationData":[OSD([subQ1])],"isStart":false}),subQ0]})])]});}
            var Q7;
            {var subQ0=sQuery(id+"F11.wireOp",EDGE,"E62.0");var subQ1=sQuery(id+"F0.wireOp",EDGE,"E2");Q7=makeQuery(id+"F14.opExtrude","SWEPT_EDGE",EDGE,{"disambiguationData":[OSD([subQ1,subQ0]),TDD([makeQuery(id+"F11.imprint","INTERSECT",VERTEX,{"derivedFrom":[makeQuery(id+"F1.opExtrude","CAP_EDGE",EDGE,{"disambiguationData":[OSD([subQ1])],"isStart":false}),subQ0]})])]});}
            fillet(context, id + "F15", {"entities" : qUnion([Q0, Q1, Q2, Q3, Q4, Q5, Q6, Q7]), "radius" : 2 * mm, "tangentPropagation" : true, "allowEdgeOverflow" : false});
        }
    });
